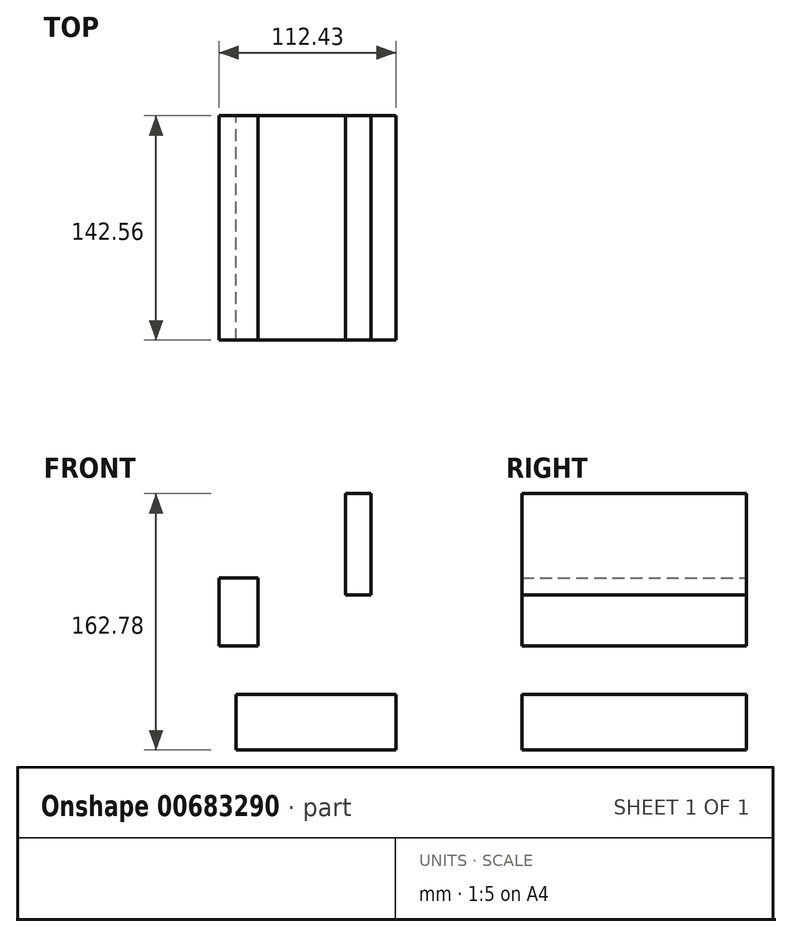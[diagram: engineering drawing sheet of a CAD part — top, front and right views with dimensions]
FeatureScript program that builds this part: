
annotation { "Feature Type Name" : "Feature", "Feature Type Description" : "" }
export const myFeature = defineFeature(function(context is Context, id is Id, definition is map)
    precondition{}
    {
        {
            var Q0;
            Q0=qCreatedBy(makeId("Front.planeOp"),FACE);
            var sketch = newSketch(context, id + "F0", { "sketchPlane" : qUnion([Q0])});
            skLineSegment(sketch, "E0.bottom", {"start": v(-50.84, 17.6) * mm, "end": v(50.84, 17.6) * mm});
            skLineSegment(sketch, "E0.top", {"start": v(-50.84, -17.6) * mm, "end": v(50.84, -17.6) * mm});
            skLineSegment(sketch, "E0.left", {"start": v(-50.84, 17.6) * mm, "end": v(-50.84, -17.6) * mm});
            skLineSegment(sketch, "E0.right", {"start": v(50.84, 17.6) * mm, "end": v(50.84, -17.6) * mm});
            skPoint(sketch, "E0.middle", {"position": v(0, 0) * mm});
            skLineSegment(sketch, "E1.bottom", {"start": v(-61.6, 91.53) * mm, "end": v(-36.9, 91.53) * mm});
            skLineSegment(sketch, "E1.top", {"start": v(-61.6, 48.52) * mm, "end": v(-36.9, 48.52) * mm});
            skLineSegment(sketch, "E1.left", {"start": v(-61.6, 91.53) * mm, "end": v(-61.6, 48.52) * mm});
            skLineSegment(sketch, "E1.right", {"start": v(-36.9, 91.53) * mm, "end": v(-36.9, 48.52) * mm});
            skPoint(sketch, "E1.middle", {"position": v(-49.25, 70.02) * mm});
            skLineSegment(sketch, "E2.bottom", {"start": v(34.92, 80.66) * mm, "end": v(18.85, 80.66) * mm});
            skLineSegment(sketch, "E2.top", {"start": v(34.92, 145.18) * mm, "end": v(18.85, 145.18) * mm});
            skLineSegment(sketch, "E2.left", {"start": v(34.92, 80.66) * mm, "end": v(34.92, 145.18) * mm});
            skLineSegment(sketch, "E2.right", {"start": v(18.85, 80.66) * mm, "end": v(18.85, 145.18) * mm});
            skPoint(sketch, "E2.middle", {"position": v(26.89, 112.92) * mm});
            skLineSegment(sketch, "E3", {"start": v(50.84, 17.6) * mm, "end": v(-36.9, 91.53) * mm});
            skArc(sketch, "E4", {"start": v(-36.9, 91.53) * mm, "mid": v(-38.81, 149.31) * mm, "end": v(18.85, 145.18) * mm});
            skLineSegment(sketch, "E5.0", {"start": v(54.93, 22.46) * mm, "end": v(-32.81, 96.39) * mm});
            skSolve(sketch);
        }
        {
            var Q0;
            Q0=makeQuery(id+"F0.imprint","IMPRINT",FACE,{"disambiguationData":[TD([[makeQuery(id+"F0.imprint","IMPRINT",EDGE,{"derivedFrom":sQuery(id+"F0.wireOp",EDGE,"E2.bottom")}),-1.0]])]});
            var Q1;
            Q1=makeQuery(id+"F0.imprint","IMPRINT",FACE,{"disambiguationData":[TD([[makeQuery(id+"F0.imprint","IMPRINT",EDGE,{"derivedFrom":sQuery(id+"F0.wireOp",EDGE,"E1.bottom")}),-1.0]])]});
            var Q2;
            Q2=makeQuery(id+"F0.imprint","IMPRINT",FACE,{"disambiguationData":[TD([[makeQuery(id+"F0.imprint","IMPRINT",EDGE,{"derivedFrom":sQuery(id+"F0.wireOp",EDGE,"E0.bottom")}),-1.0]])]});
            extrude(context, id + "F1", {"entities" : qUnion([Q0, Q1, Q2]), "depth" : 142.56 * mm, "offsetDistance" : 25.4 * mm});
        }
    });
